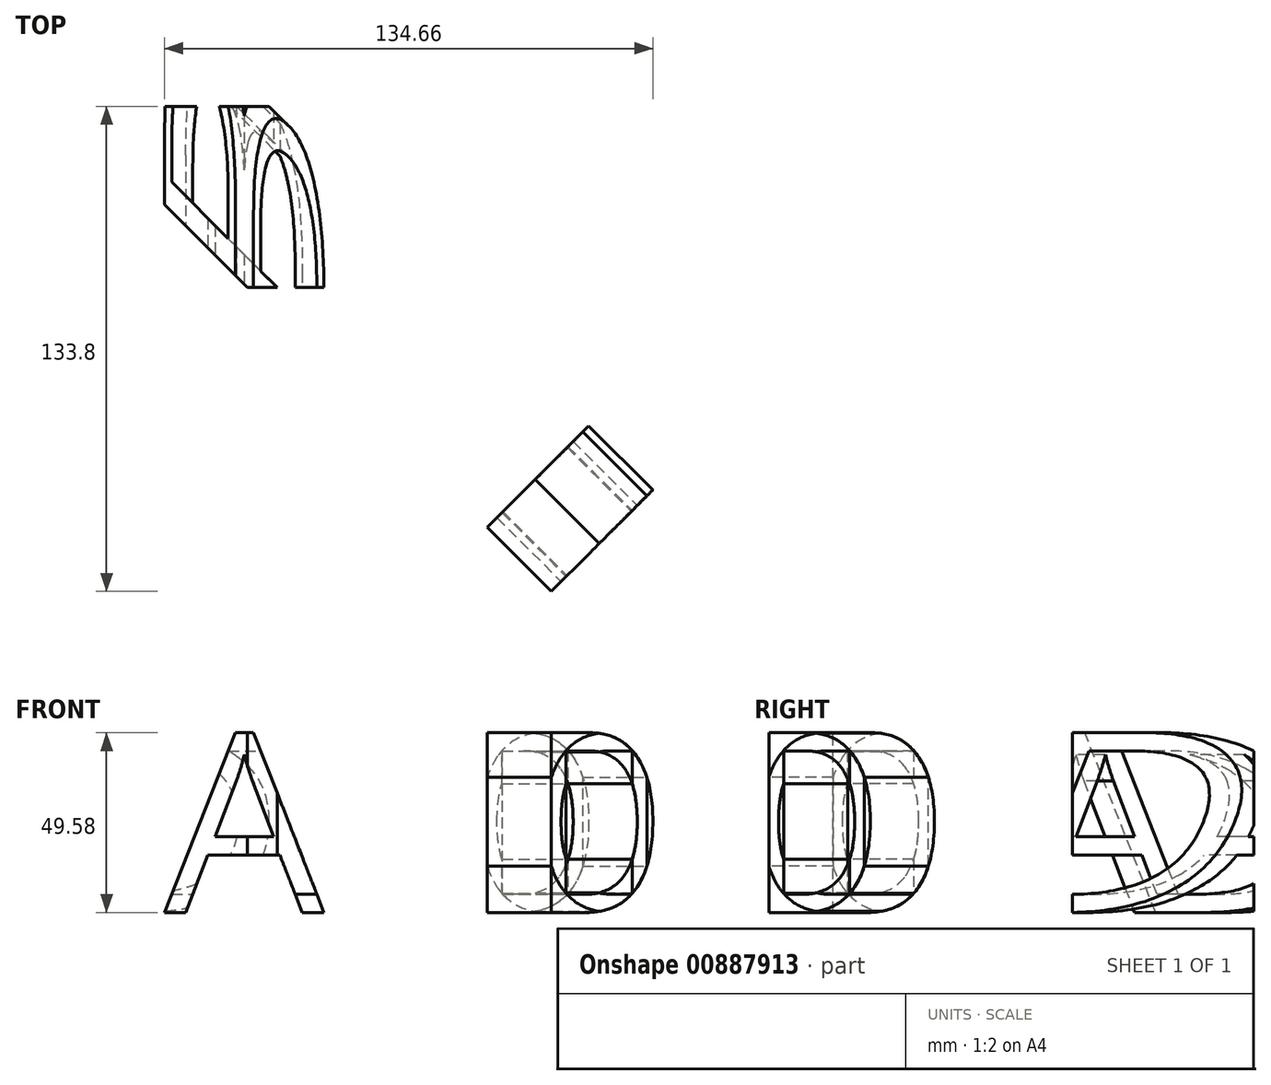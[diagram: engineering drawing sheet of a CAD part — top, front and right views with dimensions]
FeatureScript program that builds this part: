
annotation { "Feature Type Name" : "Feature", "Feature Type Description" : "" }
export const myFeature = defineFeature(function(context is Context, id is Id, definition is map)
    precondition{}
    {
        {
            var Q0;
            Q0=qCreatedBy(makeId("Top.planeOp"),FACE);
            var sketch = newSketch(context, id + "F0", { "sketchPlane" : qUnion([Q0])});
            skLineSegment(sketch, "E0.bottom", {"start": v(-25, -25) * mm, "end": v(25, -25) * mm});
            skLineSegment(sketch, "E0.top", {"start": v(-25, 25) * mm, "end": v(25, 25) * mm});
            skLineSegment(sketch, "E0.left", {"start": v(-25, -25) * mm, "end": v(-25, 25) * mm});
            skLineSegment(sketch, "E0.right", {"start": v(25, -25) * mm, "end": v(25, 25) * mm});
            skPoint(sketch, "E0.middle", {"position": v(0, 0) * mm});
            skLineSegment(sketch, "E1", {"start": v(-25, -122.02) * mm, "end": v(25, -122.02) * mm});
            skLineSegment(sketch, "E2", {"start": v(63.12, 113.12) * mm, "end": v(113.12, 63.12) * mm});
            skLineSegment(sketch, "E3", {"start": v(120.1, 25) * mm, "end": v(120.1, -25) * mm});
            skLineSegment(sketch, "E4", {"start": v(120.63, -70.63) * mm, "end": v(70.63, -120.63) * mm});
            skLineSegment(sketch, "E5", {"start": v(0, 0) * mm, "end": v(0, -122.02) * mm, "construction": true});
            skLineSegment(sketch, "E6", {"start": v(95.63, -95.63) * mm, "end": v(0, 0) * mm, "construction": true});
            skLineSegment(sketch, "E7", {"start": v(120.1, 0) * mm, "end": v(0, 0) * mm, "construction": true});
            skLineSegment(sketch, "E8", {"start": v(88.12, 88.12) * mm, "end": v(0, 0) * mm, "construction": true});
            skLineSegment(sketch, "E9", {"start": v(25, 25) * mm, "end": v(120.63, -70.63) * mm, "construction": true});
            skLineSegment(sketch, "E10", {"start": v(120.1, 25) * mm, "end": v(25, 25) * mm, "construction": true});
            skLineSegment(sketch, "E11", {"start": v(63.12, 113.12) * mm, "end": v(-25, 25) * mm, "construction": true});
            skLineSegment(sketch, "E12", {"start": v(25, -122.02) * mm, "end": v(25, -25) * mm, "construction": true});
            skSolve(sketch);
        }
        {
            var Q0;
            Q0=sQuery(id+"F0.wireOp",VERTEX,"E5.end");
            var Q1;
            Q1=sQuery(id+"F0.wireOp",EDGE,"E5");
            cPlane(context, id + "F1", {"entities" : qUnion([Q0, Q1]), "cplaneType" : CPlaneType.LINE_POINT, "offset" : 25 * mm, "width" : 150 * mm, "height" : 150 * mm});
        }
        {
            var Q0;
            Q0=sQuery(id+"F0.wireOp",EDGE,"E6");
            var Q1;
            Q1=sQuery(id+"F0.wireOp",VERTEX,"E6.start");
            cPlane(context, id + "F2", {"entities" : qUnion([Q0, Q1]), "cplaneType" : CPlaneType.LINE_POINT, "offset" : 25 * mm, "width" : 150 * mm, "height" : 150 * mm});
        }
        {
            var Q0;
            Q0=sQuery(id+"F0.wireOp",EDGE,"E7");
            var Q1;
            Q1=sQuery(id+"F0.wireOp",VERTEX,"E7.start");
            cPlane(context, id + "F3", {"entities" : qUnion([Q0, Q1]), "cplaneType" : CPlaneType.LINE_POINT, "offset" : 25 * mm, "width" : 150 * mm, "height" : 150 * mm});
        }
        {
            var Q0;
            Q0=sQuery(id+"F0.wireOp",EDGE,"E2");
            cPoint(context, id + "F4", {"entities" : qUnion([Q0]), "parameter" : 0.5});
        }
        {
            var Q0;
            Q0=sQuery(id+"F0.wireOp",EDGE,"E8");
            var Q1;
            Q1 = qCreatedBy(id + "F4" ,VERTEX);
            cPlane(context, id + "F5", {"entities" : qUnion([Q0, Q1]), "cplaneType" : CPlaneType.LINE_POINT, "offset" : 25 * mm, "width" : 150 * mm, "height" : 150 * mm});
        }
        {
            var Q0;
            Q0=makeQuery(id+"F0.imprint","IMPRINT",FACE,{"disambiguationData":[TD([[makeQuery(id+"F0.imprint","IMPRINT",EDGE,{"derivedFrom":sQuery(id+"F0.wireOp",EDGE,"E0.bottom")}),1.0]])]});
            extrude(context, id + "F6", {"entities" : qUnion([Q0]), "depth" : 100 * mm, "offsetDistance" : 25 * mm});
        }
        {
            var Q0;
            Q0=qCreatedBy(id+"F1.planeOp",FACE);
            var sketch = newSketch(context, id + "F7", { "sketchPlane" : qUnion([Q0])});
            skLineSegment(sketch, "E13.0", {"start": v(-25, 0) * mm, "end": v(25, 0) * mm});
            skText(sketch, "E14", { "text": "A", "fontName": "OpenSans-Regular.ttf"});
            const initialGuessF7  = {"E14": [-0.02422, 0, 1, 0, 0.05]};
            skSetInitialGuess(sketch, initialGuessF7);
            skSolve(sketch);
        }
        {
            var Q0;
            Q0=qCreatedBy(id+"F2.planeOp",FACE);
            var sketch = newSketch(context, id + "F8", { "sketchPlane" : qUnion([Q0])});
            skLineSegment(sketch, "E15.0", {"start": v(-35.36, 0) * mm, "end": v(35.36, 0) * mm});
            skText(sketch, "E16", { "text": "D", "fontName": "OpenSans-Regular.ttf"});
            const initialGuessF8  = {"E16": [-0.02544, 0, 1, 0, 0.05]};
            skSetInitialGuess(sketch, initialGuessF8);
            skSolve(sketch);
        }
        {
            var Q0;
            Q0=makeQuery(id+"F7.imprint","IMPRINT",FACE,{"disambiguationData":[TD([[makeQuery(id+"F7.imprint","IMPRINT",EDGE,{"derivedFrom":sQuery(id+"F7.wireOp",EDGE,"E14.sketch_text.stroke-0")}),-1.0]])]});
            extrude(context, id + "F9", {"entities" : qUnion([Q0]), "operationType" : NewBodyOperationType.INTERSECT, "endBound" : BoundingType.THROUGH_ALL, "oppositeDirection" : true, "depth" : 25 * mm, "offsetDistance" : 25 * mm});
        }
        {
            var Q0;
            Q0=makeQuery(id+"F8.imprint","IMPRINT",FACE,{"disambiguationData":[TD([[makeQuery(id+"F8.imprint","IMPRINT",EDGE,{"derivedFrom":sQuery(id+"F8.wireOp",EDGE,"E16.sketch_text.stroke-0")}),-1.0]])]});
            extrude(context, id + "F10", {"entities" : qUnion([Q0]), "depth" : 25 * mm, "offsetDistance" : 25 * mm});
        }
        {
            var Q0;
            Q0=sQuery(id+"F8.wireOp",EDGE,"E15.0");
            cPlane(context, id + "F11", {"entities" : qUnion([Q0]), "cplaneType" : CPlaneType.MID_PLANE, "offset" : 25 * mm, "width" : 150 * mm, "height" : 150 * mm});
        }
        {
            var Q0;
            Q0=makeQuery(id+"F10.opExtrude","SWEPT_BODY",BODY,{"disambiguationData":[OSD([sQuery(id+"F8.wireOp",EDGE,"E16.sketch_text.stroke-0"),sQuery(id+"F8.wireOp",EDGE,"E16.sketch_text.stroke-1"),sQuery(id+"F8.wireOp",EDGE,"E16.sketch_text.stroke-2"),sQuery(id+"F8.wireOp",EDGE,"E16.sketch_text.stroke-3"),sQuery(id+"F8.wireOp",EDGE,"E16.sketch_text.stroke-4"),sQuery(id+"F8.wireOp",EDGE,"E16.sketch_text.stroke-5"),sQuery(id+"F8.wireOp",EDGE,"E16.sketch_text.stroke-6"),sQuery(id+"F8.wireOp",EDGE,"E16.sketch_text.stroke-7"),sQuery(id+"F8.wireOp",EDGE,"E16.sketch_text.stroke-8"),sQuery(id+"F8.wireOp",EDGE,"E16.sketch_text.stroke-9"),sQuery(id+"F8.wireOp",EDGE,"E16.sketch_text.stroke-10"),sQuery(id+"F8.wireOp",EDGE,"E16.sketch_text.stroke-11"),sQuery(id+"F8.wireOp",EDGE,"E16.sketch_text.stroke-12"),sQuery(id+"F8.wireOp",EDGE,"E16.sketch_text.stroke-13")])]});
            var Q1;
            Q1=qCreatedBy(id+"F11.planeOp",FACE);
            mirror(context, id + "F12", {"entities" : qUnion([Q0]), "mirrorPlane" : qUnion([Q1])});
        }
        {
            var Q0;
            Q0=makeQuery(id+"F12.opPattern","COPY",FACE,{"derivedFrom":makeQuery(id+"F10.opExtrude","CAP_FACE",FACE,{"disambiguationData":[OSD([sQuery(id+"F8.wireOp",EDGE,"E16.sketch_text.stroke-0"),sQuery(id+"F8.wireOp",EDGE,"E16.sketch_text.stroke-1"),sQuery(id+"F8.wireOp",EDGE,"E16.sketch_text.stroke-2"),sQuery(id+"F8.wireOp",EDGE,"E16.sketch_text.stroke-3"),sQuery(id+"F8.wireOp",EDGE,"E16.sketch_text.stroke-4"),sQuery(id+"F8.wireOp",EDGE,"E16.sketch_text.stroke-5"),sQuery(id+"F8.wireOp",EDGE,"E16.sketch_text.stroke-6"),sQuery(id+"F8.wireOp",EDGE,"E16.sketch_text.stroke-7"),sQuery(id+"F8.wireOp",EDGE,"E16.sketch_text.stroke-8"),sQuery(id+"F8.wireOp",EDGE,"E16.sketch_text.stroke-9"),sQuery(id+"F8.wireOp",EDGE,"E16.sketch_text.stroke-10"),sQuery(id+"F8.wireOp",EDGE,"E16.sketch_text.stroke-11"),sQuery(id+"F8.wireOp",EDGE,"E16.sketch_text.stroke-12"),sQuery(id+"F8.wireOp",EDGE,"E16.sketch_text.stroke-13")])],"isStart":true}),"instanceName":"1"});
            extrude(context, id + "F13", {"entities" : qUnion([Q0]), "operationType" : NewBodyOperationType.INTERSECT, "endBound" : BoundingType.THROUGH_ALL, "oppositeDirection" : true, "depth" : 25 * mm, "offsetDistance" : 25 * mm});
        }
    });
